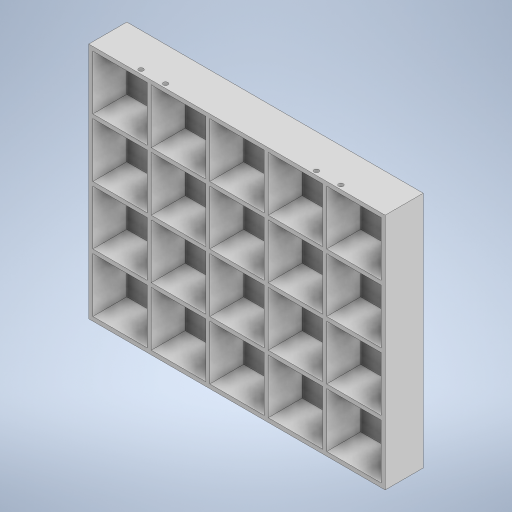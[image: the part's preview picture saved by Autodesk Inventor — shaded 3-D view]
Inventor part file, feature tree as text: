
AUTODESK INVENTOR PART (.ipt)
format: ipt  version: 2023.5 (Build 275446000, 446)  size: 401,920 bytes
history: native  units: in
note: dims shown in document units (in); Inventor stores cm internally (conversion verified against a paired STEP export)
features: extrude x3, sketch x3
ambient origin geometry x8: Origin, YZ Plane, XZ Plane, XY Plane, X Axis, Y Axis, Z Axis, Center Point
bodies: Solid1 (feature_tree)
feature tree (6):
  extrude  "Extrusion1"  Depth=6.8898in
  extrude  "Extrusion2"  TaperAngle=0.0deg  [1 undecoded]
  extrude  "Extrusion3"  Depth=0.1181in
  sketch  "Sketch1"  dims[d0=8.5827in d1=6.8898in]
  sketch  "Sketch2"  dims[d2=1.1024in d3=0.0in]
  sketch  "Sketch3"  dims[d4=1.5748in d5=0.1181in d6=0.1181in d7=1.5748in d8=1.9685in d10=1.6929in d11=1.5748in d13=1.6929in d16=0.9843in d17=0.0in d20=0.1181in d21=0.1299in d22=0.3543in d23=0.1299in d24=0.3543in d25=0.1299in d27=0.3543in d30=0.1181in d31=0.1299in d32=0.3543in d33=0.3937in d34=0.0in]
note: 1 required parameter value undecoded (feature->parameter linkage not recoverable at this tier; creation-order binding heuristic only, values carry confidence <= 0.55)
